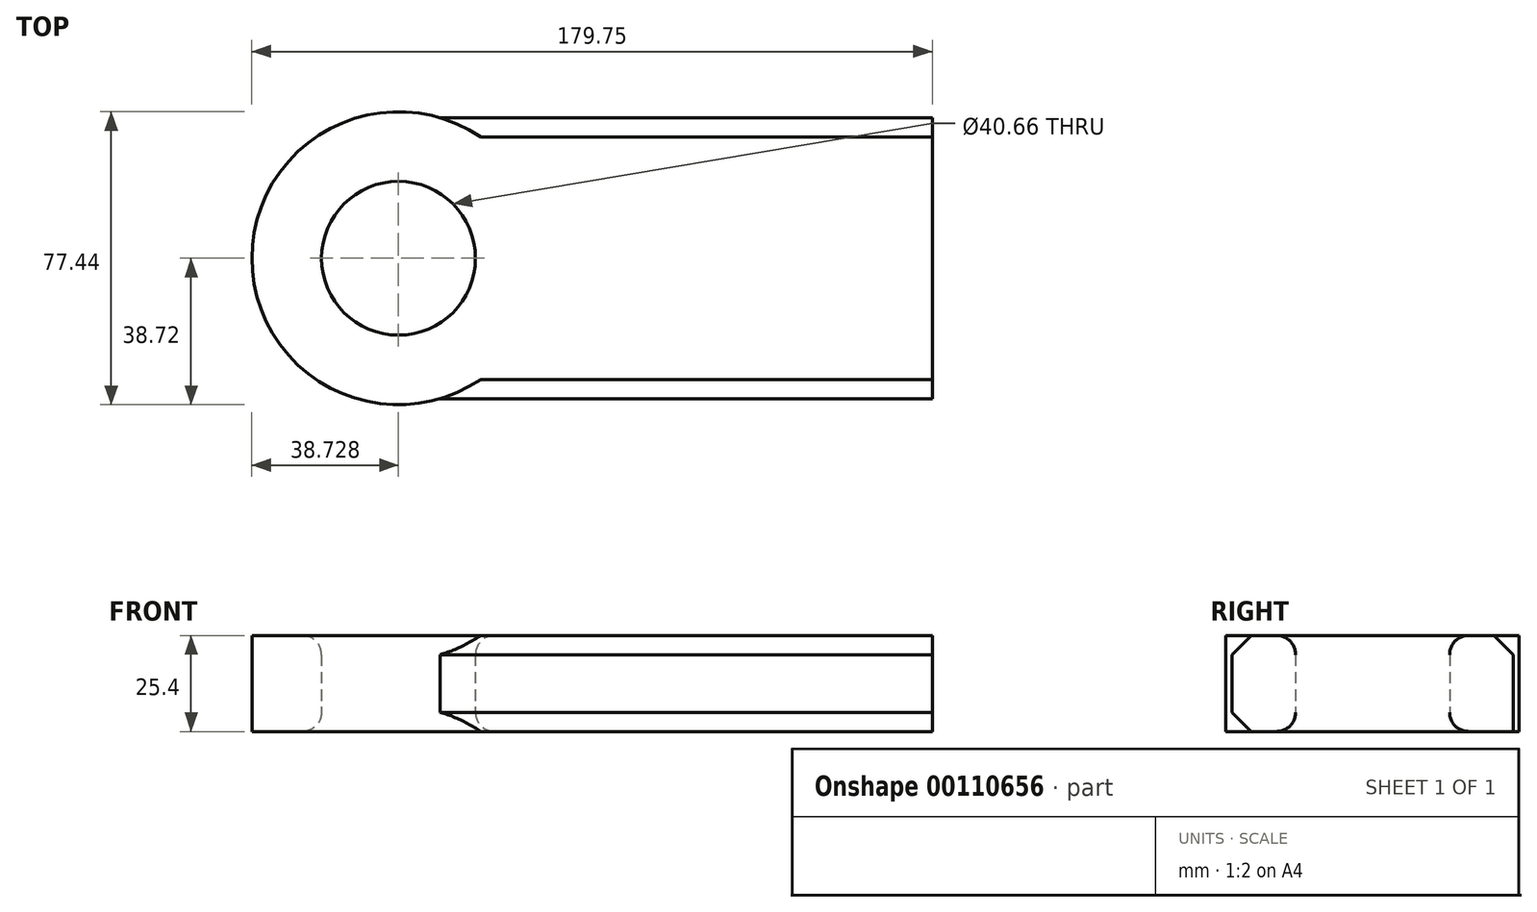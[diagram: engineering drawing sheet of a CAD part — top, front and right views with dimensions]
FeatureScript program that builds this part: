
annotation { "Feature Type Name" : "Feature", "Feature Type Description" : "" }
export const myFeature = defineFeature(function(context is Context, id is Id, definition is map)
    precondition{}
    {
        {
            var Q0;
            Q0=qCreatedBy(makeId("Top.planeOp"),FACE);
            var sketch = newSketch(context, id + "F0", { "sketchPlane" : qUnion([Q0])});
            skLineSegment(sketch, "E0.bottom", {"start": v(-76.04, -37.11) * mm, "end": v(76.04, -37.11) * mm});
            skLineSegment(sketch, "E0.top", {"start": v(-76.04, 37.11) * mm, "end": v(76.04, 37.11) * mm});
            skLineSegment(sketch, "E0.left", {"start": v(-76.04, -37.11) * mm, "end": v(-76.04, 37.11) * mm});
            skLineSegment(sketch, "E0.right", {"start": v(76.04, -37.11) * mm, "end": v(76.04, 37.11) * mm});
            skPoint(sketch, "E0.middle", {"position": v(0, 0) * mm});
            skPoint(sketch, "E1.centerSnap0", {"position": v(-76.04, 0) * mm});
            skCircle(sketch, "E2", {"center": v(-64.98, 0) * mm, "radius": 38.72 * mm});
            skCircle(sketch, "E3", {"center": v(-64.98, 0) * mm, "radius": 20.33 * mm});
            skSolve(sketch);
        }
        {
            var Q0;
            Q0 = qSketchRegion(id + "F0", true);
            extrude(context, id + "F1", {"entities" : qUnion([Q0]), "depth" : 25.4 * mm});
        }
        {
            var Q0;
            Q0=makeQuery(id+"F1.opExtrude","CAP_EDGE",EDGE,{"disambiguationData":[OSD([sQuery(id+"F0.wireOp",EDGE,"E3")])],"isStart":false});
            fillet(context, id + "F2", {"entities" : qUnion([Q0]), "radius" : 5.08 * mm, "tangentPropagation" : true, "allowEdgeOverflow" : false});
        }
        {
            var Q0;
            Q0=makeQuery(id+"F1.opExtrude","CAP_EDGE",EDGE,{"disambiguationData":[OSD([sQuery(id+"F0.wireOp",EDGE,"E3")])],"isStart":true});
            fillet(context, id + "F3", {"entities" : qUnion([Q0]), "radius" : 5.08 * mm, "tangentPropagation" : true, "allowEdgeOverflow" : false});
        }
        {
            var Q0;
            Q0=makeQuery(id+"F1.opExtrude","CAP_EDGE",EDGE,{"disambiguationData":[OSD([sQuery(id+"F0.wireOp",EDGE,"E0.bottom")])],"isStart":false});
            var Q1;
            Q1=makeQuery(id+"F1.opExtrude","CAP_EDGE",EDGE,{"disambiguationData":[OSD([sQuery(id+"F0.wireOp",EDGE,"E0.top")])],"isStart":false});
            var Q2;
            Q2=makeQuery(id+"F1.opExtrude","CAP_EDGE",EDGE,{"disambiguationData":[OSD([sQuery(id+"F0.wireOp",EDGE,"E0.bottom")])],"isStart":true});
            chamfer(context, id + "F4", {"entities" : qUnion([Q0, Q1, Q2]), "width" : 5.08 * mm, "tangentPropagation" : true});
        }
    });
